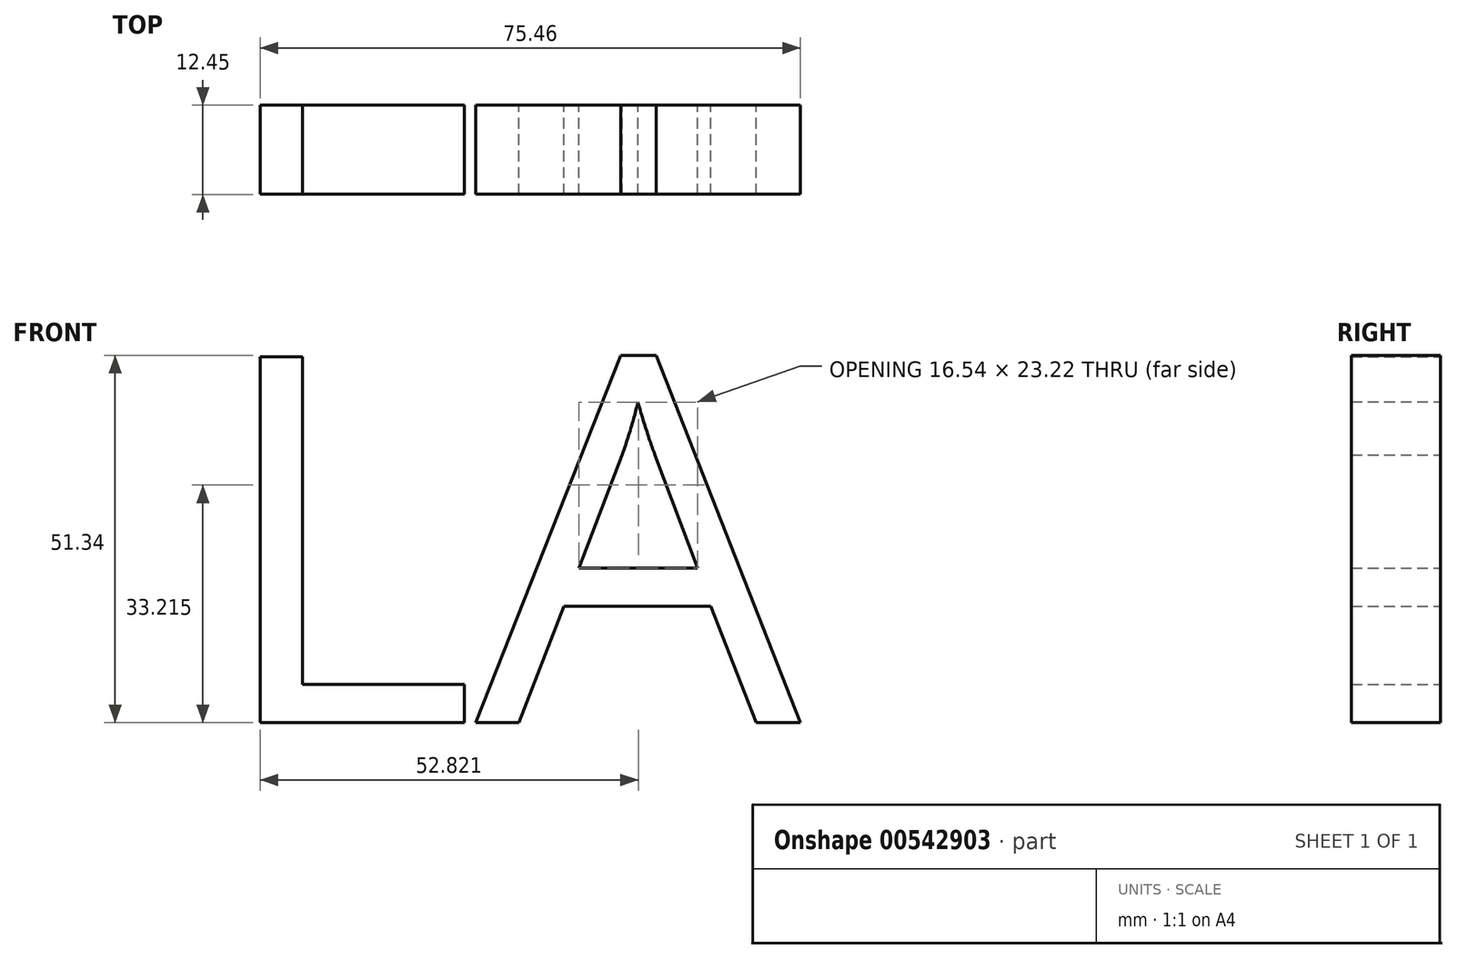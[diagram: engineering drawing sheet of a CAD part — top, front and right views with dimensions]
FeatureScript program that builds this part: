
annotation { "Feature Type Name" : "Feature", "Feature Type Description" : "" }
export const myFeature = defineFeature(function(context is Context, id is Id, definition is map)
    precondition{}
    {
        {
            var Q0;
            Q0=qCreatedBy(makeId("Front.planeOp"),FACE);
            var sketch = newSketch(context, id + "F0", { "sketchPlane" : qUnion([Q0])});
            skText(sketch, "E0", { "text": "LA", "fontName": "OpenSans-Regular.ttf"});
            skLineSegment(sketch, "E1.bottom", {"start": v(-52.9, 38.22) * mm, "end": v(52.3, 38.22) * mm, "construction": true});
            skLineSegment(sketch, "E1.top", {"start": v(-52.9, -24.57) * mm, "end": v(52.3, -24.57) * mm, "construction": true});
            skLineSegment(sketch, "E1.left", {"start": v(-52.9, 38.22) * mm, "end": v(-52.9, -24.57) * mm, "construction": true});
            skLineSegment(sketch, "E1.right", {"start": v(52.3, 38.22) * mm, "end": v(52.3, -24.57) * mm, "construction": true});
            const initialGuessF0  = {"E0": [-0.04378, -0.01848, 1, 0, 0.05156]};
            skSetInitialGuess(sketch, initialGuessF0);
            skSolve(sketch);
        }
        {
            var Q0;
            Q0 = qSketchRegion(id + "F0", true);
            extrude(context, id + "F1", {"entities" : qUnion([Q0]), "depth" : 12.45 * mm, "offsetDistance" : 25.4 * mm});
        }
    });
